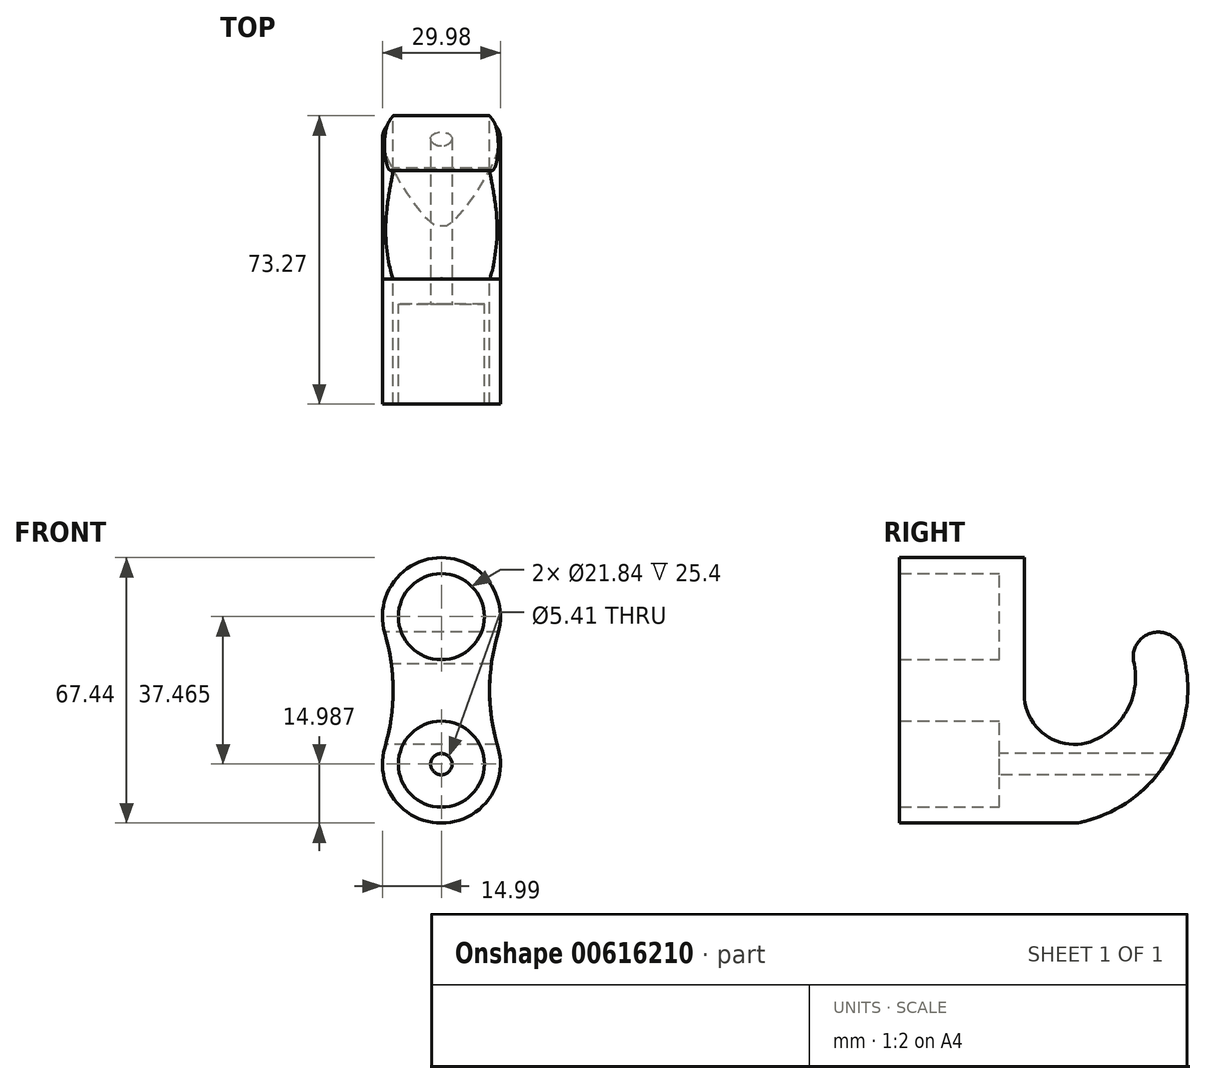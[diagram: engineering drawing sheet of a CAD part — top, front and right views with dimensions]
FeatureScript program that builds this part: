
annotation { "Feature Type Name" : "Feature", "Feature Type Description" : "" }
export const myFeature = defineFeature(function(context is Context, id is Id, definition is map)
    precondition{}
    {
        {
            var Q0;
            Q0=qCreatedBy(makeId("Front.planeOp"),FACE);
            var sketch = newSketch(context, id + "F0", { "sketchPlane" : qUnion([Q0])});
            skCircle(sketch, "E0", {"center": v(0, 18.73) * mm, "radius": 10.92 * mm});
            skCircle(sketch, "E1", {"center": v(0, -18.73) * mm, "radius": 10.92 * mm});
            skLineSegment(sketch, "E2", {"start": v(0, 18.73) * mm, "end": v(0, -18.73) * mm, "construction": true});
            skCircle(sketch, "E3", {"center": v(0, 18.73) * mm, "radius": 14.99 * mm});
            skCircle(sketch, "E4", {"center": v(0, -18.73) * mm, "radius": 14.99 * mm});
            skArc(sketch, "E5", {"start": v(-14.37, -14.47) * mm, "mid": v(-12.26, 0) * mm, "end": v(-14.37, 14.47) * mm});
            skArc(sketch, "E6", {"start": v(14.37, 14.47) * mm, "mid": v(12.26, 0) * mm, "end": v(14.37, -14.47) * mm});
            skSolve(sketch);
        }
        {
            var Q0;
            {var subQ0=sQuery(id+"F0.wireOp",EDGE,"E5");Q0=makeQuery(id+"F0.imprint","IMPRINT",FACE,{"disambiguationData":[TD([[makeQuery(id+"F0.imprint","IMPRINT",EDGE,{"derivedFrom":subQ0}),-1.0]])]});}
            var Q1;
            Q1=makeQuery(id+"F0.imprint","IMPRINT",FACE,{"disambiguationData":[TD([[makeQuery(id+"F0.imprint","IMPRINT",EDGE,{"derivedFrom":sQuery(id+"F0.wireOp",EDGE,"E0")}),-1.0]])]});
            var Q2;
            Q2=makeQuery(id+"F0.imprint","IMPRINT",FACE,{"disambiguationData":[TD([[makeQuery(id+"F0.imprint","IMPRINT",EDGE,{"derivedFrom":sQuery(id+"F0.wireOp",EDGE,"E1")}),-1.0]])]});
            extrude(context, id + "F1", {"entities" : qUnion([Q0, Q1, Q2]), "depth" : 25.4 * mm, "offsetDistance" : 25.4 * mm});
        }
        {
            var Q0;
            Q0=qSketchRegion(id+"F0",true);
            var Q1;
            Q1=makeQuery(id+"F0.imprint","IMPRINT",FACE,{"disambiguationData":[TD([[makeQuery(id+"F0.imprint","IMPRINT",EDGE,{"derivedFrom":sQuery(id+"F0.wireOp",EDGE,"E0")}),1.0]])]});
            var Q2;
            Q2=makeQuery(id+"F0.imprint","IMPRINT",FACE,{"disambiguationData":[TD([[makeQuery(id+"F0.imprint","IMPRINT",EDGE,{"derivedFrom":sQuery(id+"F0.wireOp",EDGE,"E1")}),1.0]])]});
            extrude(context, id + "F2", {"entities" : qUnion([Q0, Q1, Q2]), "operationType" : NewBodyOperationType.ADD, "oppositeDirection" : true, "depth" : 6.35 * mm});
        }
        {
            var Q0;
            Q0=qCreatedBy(makeId("Right.planeOp"),FACE);
            var sketch = newSketch(context, id + "F3", { "sketchPlane" : qUnion([Q0])});
            skArc(sketch, "E7", {"start": v(6.35, -33.67) * mm, "mid": v(38.78, -23) * mm, "end": v(46.44, 10.26) * mm});
            skArc(sketch, "E8", {"start": v(0, 0) * mm, "mid": v(20.46, -13.8) * mm, "end": v(34.26, 6.66) * mm});
            skArc(sketch, "E9", {"start": v(46.44, 10.26) * mm, "mid": v(38.56, 14.55) * mm, "end": v(34.26, 6.66) * mm});
            skPoint(sketch, "E10", {"position": v(0, 0) * mm});
            skLineSegment(sketch, "E11", {"start": v(0, 0) * mm, "end": v(6.35, -33.67) * mm});
            skSolve(sketch);
        }
        {
            var Q0;
            Q0=makeQuery(id+"F3.imprint","IMPRINT",FACE,{"disambiguationData":[TD([[makeQuery(id+"F3.imprint","IMPRINT",EDGE,{"derivedFrom":sQuery(id+"F3.wireOp",EDGE,"E7")}),1.0]])]});
            extrude(context, id + "F4", {"entities" : qUnion([Q0]), "operationType" : NewBodyOperationType.ADD, "endBound" : BoundingType.SYMMETRIC, "depth" : 50.8 * mm});
        }
        {
            var Q0;
            Q0=qSketchRegion(id+"F0",true);
            var Q1;
            Q1=makeQuery(id+"F0.imprint","IMPRINT",FACE,{"disambiguationData":[TD([[makeQuery(id+"F0.imprint","IMPRINT",EDGE,{"derivedFrom":sQuery(id+"F0.wireOp",EDGE,"E1")}),1.0]])]});
            var Q2;
            Q2=makeQuery(id+"F0.imprint","IMPRINT",FACE,{"disambiguationData":[TD([[makeQuery(id+"F0.imprint","IMPRINT",EDGE,{"derivedFrom":sQuery(id+"F0.wireOp",EDGE,"E0")}),1.0]])]});
            extrude(context, id + "F5", {"entities" : qUnion([Q0, Q1, Q2]), "operationType" : NewBodyOperationType.INTERSECT, "oppositeDirection" : true, "depth" : 76.2 * mm});
        }
        {
            var Q0;
            Q0=makeQuery(id+"F0.imprint","IMPRINT",FACE,{"disambiguationData":[TD([[makeQuery(id+"F0.imprint","IMPRINT",EDGE,{"derivedFrom":sQuery(id+"F0.wireOp",EDGE,"E0")}),-1.0]])]});
            var Q1;
            {var subQ0=sQuery(id+"F0.wireOp",EDGE,"E5");Q1=makeQuery(id+"F0.imprint","IMPRINT",FACE,{"disambiguationData":[TD([[makeQuery(id+"F0.imprint","IMPRINT",EDGE,{"derivedFrom":subQ0}),-1.0]])]});}
            var Q2;
            Q2=makeQuery(id+"F0.imprint","IMPRINT",FACE,{"disambiguationData":[TD([[makeQuery(id+"F0.imprint","IMPRINT",EDGE,{"derivedFrom":sQuery(id+"F0.wireOp",EDGE,"E1")}),-1.0]])]});
            var Q3;
            Q3=sQuery(id+"F0.wireOp",EDGE,"E3");
            extrude(context, id + "F6", {"entities" : qUnion([Q0, Q1, Q2]), "operationType" : NewBodyOperationType.ADD, "surfaceEntities" : qUnion([Q3]), "depth" : 25.4 * mm});
        }
        {
            var Q0;
            Q0=sQuery(id+"F0.wireOp",VERTEX,"E4.center");
            var Q1;
            Q1=makeQuery(id+"F1.opExtrude","SWEPT_BODY",BODY,{"disambiguationData":[OSD([sQuery(id+"F0.wireOp",EDGE,"E0"),sQuery(id+"F0.wireOp",EDGE,"E1"),sQuery(id+"F0.wireOp",EDGE,"E3"),sQuery(id+"F0.wireOp",EDGE,"E4"),sQuery(id+"F0.wireOp",EDGE,"E5"),sQuery(id+"F0.wireOp",EDGE,"E6")])]});
            hole(context, id + "F7", {"style" : HoleStyle.SIMPLE, "endStyle" : HoleEndStyle.THROUGH, "standardTappedOrClearance" : lookupTablePath({ "standard" : "ANSI", "engagement" : "75%", "pitch" : "28 tpi", "size" : "1/4", "type" : "Tapped" }), "standardBlindInLast" : lookupTablePath({ "standard" : "ANSI", "engagement" : "75%", "pitch" : "28 tpi", "size" : "1/4", "type" : "Tapped" }), "holeDiameter" : 5.4 * mm, "locations" : qUnion([Q0]), "scope" : qUnion([Q1]), "isTappedThrough" : true, "majorDiameter" : 6.35 * mm, "showTappedDepth" : true});
        }
        {
            var Q0;
            Q0=makeQuery(id+"F4.boolean.opBoolean","INTERSECT",EDGE,{"derivedFrom":[makeQuery(id+"F2.opExtrude","CAP_FACE",FACE,{"disambiguationData":[OSD([sQuery(id+"F0.wireOp",EDGE,"E3"),sQuery(id+"F0.wireOp",EDGE,"E4"),sQuery(id+"F0.wireOp",EDGE,"E5"),sQuery(id+"F0.wireOp",EDGE,"E6")])],"isStart":false}),makeQuery(id+"F4.opExtrude","SWEPT_FACE",FACE,{"disambiguationData":[OSD([sQuery(id+"F3.wireOp",EDGE,"E8")])]})]});
            fillet(context, id + "F8", {"entities" : qUnion([Q0]), "radius" : 12.7 * mm, "tangentPropagation" : true, "allowEdgeOverflow" : false});
        }
    });
